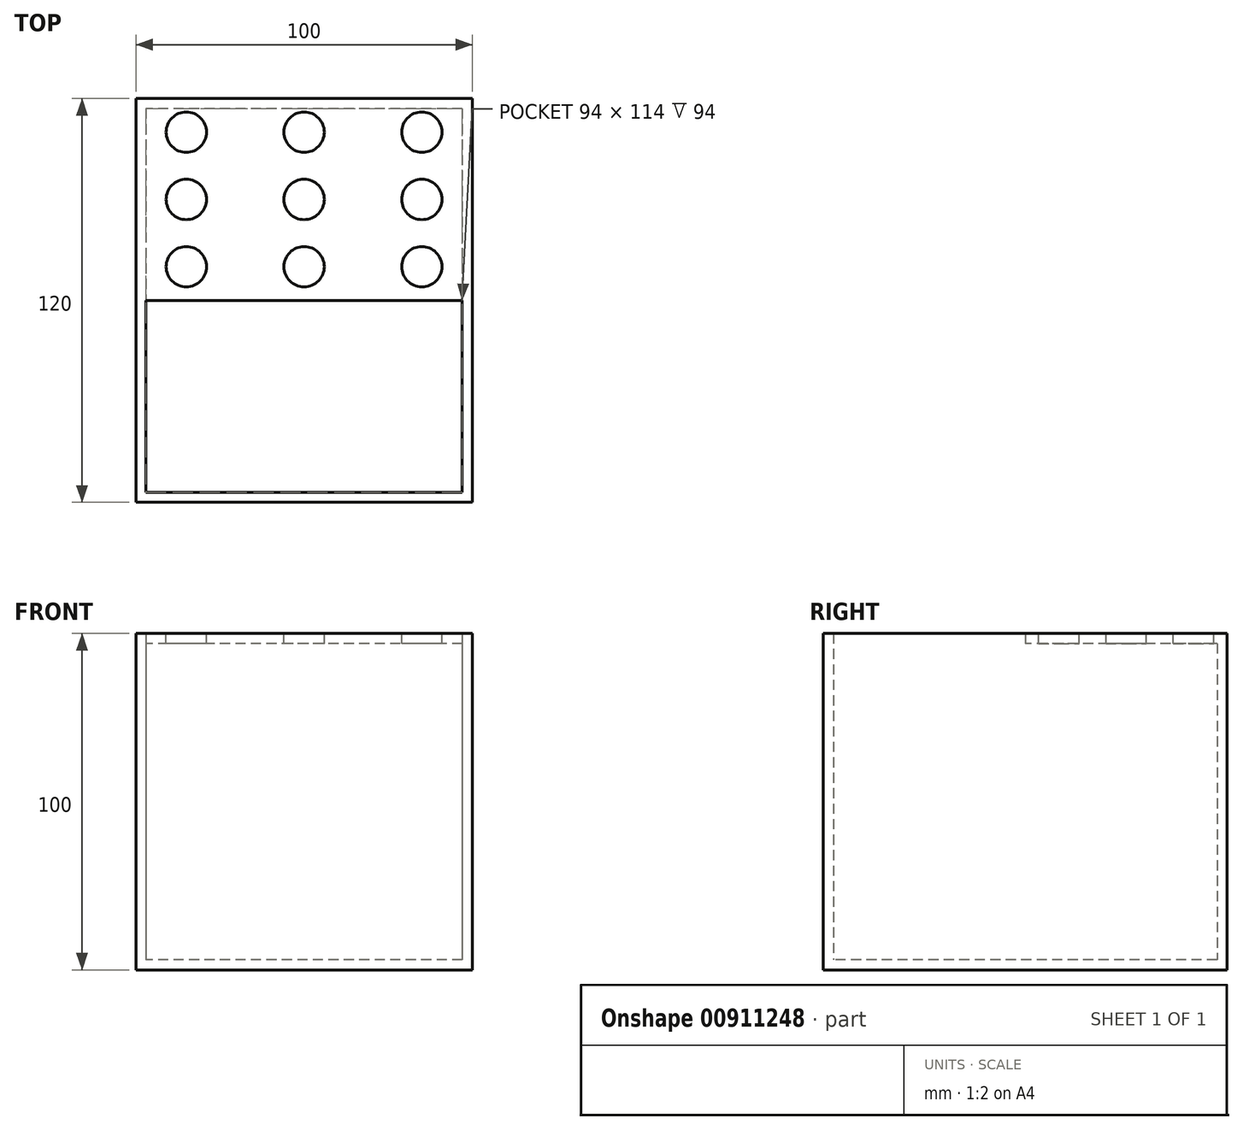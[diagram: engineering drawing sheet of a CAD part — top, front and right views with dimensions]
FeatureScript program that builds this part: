
annotation { "Feature Type Name" : "Feature", "Feature Type Description" : "" }
export const myFeature = defineFeature(function(context is Context, id is Id, definition is map)
    precondition{}
    {
        {
            var Q0;
            Q0=qCreatedBy(makeId("Top.planeOp"),FACE);
            var sketch = newSketch(context, id + "F0", { "sketchPlane" : qUnion([Q0])});
            skLineSegment(sketch, "E0.bottom", {"start": v(50, 60) * mm, "end": v(-50, 60) * mm});
            skLineSegment(sketch, "E0.top", {"start": v(50, -60) * mm, "end": v(-50, -60) * mm});
            skLineSegment(sketch, "E0.left", {"start": v(50, 60) * mm, "end": v(50, -60) * mm});
            skLineSegment(sketch, "E0.right", {"start": v(-50, 60) * mm, "end": v(-50, -60) * mm});
            skPoint(sketch, "E0.middle", {"position": v(0, 0) * mm});
            skSolve(sketch);
        }
        {
            var Q0;
            Q0 = qSketchRegion(id + "F0", true);
            extrude(context, id + "F1", {"entities" : qUnion([Q0]), "depth" : 100 * mm, "offsetDistance" : 25 * mm});
        }
        {
            var Q0;
            Q0=makeQuery(id+"F1.opExtrude","CAP_FACE",FACE,{"disambiguationData":[OSD([sQuery(id+"F0.wireOp",EDGE,"E0.bottom"),sQuery(id+"F0.wireOp",EDGE,"E0.top"),sQuery(id+"F0.wireOp",EDGE,"E0.left"),sQuery(id+"F0.wireOp",EDGE,"E0.right")])],"isStart":false});
            shell(context, id + "F2", {"entities" : qUnion([Q0]), "thickness" : 3 * mm});
        }
        {
            var Q0;
            Q0=makeQuery(id+"F1.opExtrude","CAP_FACE",FACE,{"disambiguationData":[OSD([sQuery(id+"F0.wireOp",EDGE,"E0.bottom"),sQuery(id+"F0.wireOp",EDGE,"E0.top"),sQuery(id+"F0.wireOp",EDGE,"E0.left"),sQuery(id+"F0.wireOp",EDGE,"E0.right")])],"isStart":false});
            var sketch = newSketch(context, id + "F3", { "sketchPlane" : qUnion([Q0])});
            skPoint(sketch, "E1.0", {"position": v(-50, 60) * mm});
            skLineSegment(sketch, "E2.bottom", {"start": v(-50, 60) * mm, "end": v(50, 60) * mm});
            skLineSegment(sketch, "E2.top", {"start": v(-50, 0) * mm, "end": v(50, 0) * mm});
            skLineSegment(sketch, "E2.left", {"start": v(-50, 60) * mm, "end": v(-50, 0) * mm});
            skLineSegment(sketch, "E2.right", {"start": v(50, 60) * mm, "end": v(50, 0) * mm});
            skSolve(sketch);
        }
        {
            var Q0;
            Q0 = qSketchRegion(id + "F3", true);
            extrude(context, id + "F4", {"entities" : qUnion([Q0]), "operationType" : NewBodyOperationType.ADD, "oppositeDirection" : true, "depth" : 3 * mm, "offsetDistance" : 25 * mm});
        }
        {
            var Q0;
            Q0=makeQuery(id+"F4.boolean.opBoolean","MERGE",FACE,{"derivedFrom":[makeQuery(id+"F1.opExtrude","CAP_FACE",FACE,{"disambiguationData":[OSD([sQuery(id+"F0.wireOp",EDGE,"E0.bottom"),sQuery(id+"F0.wireOp",EDGE,"E0.top"),sQuery(id+"F0.wireOp",EDGE,"E0.left"),sQuery(id+"F0.wireOp",EDGE,"E0.right")])],"isStart":false}),makeQuery(id+"F4.opExtrude","CAP_FACE",FACE,{"disambiguationData":[OSD([sQuery(id+"F3.wireOp",EDGE,"E2.bottom"),sQuery(id+"F3.wireOp",EDGE,"E2.top"),sQuery(id+"F3.wireOp",EDGE,"E2.left"),sQuery(id+"F3.wireOp",EDGE,"E2.right")])],"isStart":true})]});
            var sketch = newSketch(context, id + "F5", { "sketchPlane" : qUnion([Q0])});
            skCircle(sketch, "E3", {"center": v(0, 30) * mm, "radius": 6 * mm});
            skLineSegment(sketch, "E4", {"start": v(0, 60) * mm, "end": v(0, 0) * mm, "construction": true});
            skCircle(sketch, "E5", {"center": v(35, 30) * mm, "radius": 6 * mm});
            skCircle(sketch, "E6.MirrorC", {"center": v(-35, 30) * mm, "radius": 6 * mm});
            skCircle(sketch, "E7.0.1.0", {"center": v(-35, 50) * mm, "radius": 6 * mm});
            skCircle(sketch, "E7.0.1.1", {"center": v(0, 50) * mm, "radius": 6 * mm});
            skCircle(sketch, "E7.0.1.2", {"center": v(35, 50) * mm, "radius": 6 * mm});
            skLineSegment(sketch, "E7.direction1", {"start": v(-35, 30) * mm, "end": v(-10, 30) * mm, "construction": true});
            skLineSegment(sketch, "E7.direction2", {"start": v(-35, 30) * mm, "end": v(-35, 50) * mm, "construction": true});
            skCircle(sketch, "E8.0.1.0", {"center": v(-35, 10) * mm, "radius": 6 * mm});
            skCircle(sketch, "E8.0.1.1", {"center": v(0, 10) * mm, "radius": 6 * mm});
            skCircle(sketch, "E8.0.1.2", {"center": v(35, 10) * mm, "radius": 6 * mm});
            skLineSegment(sketch, "E8.direction2", {"start": v(-35, 30) * mm, "end": v(-35, 10) * mm, "construction": true});
            skSolve(sketch);
        }
        {
            var Q0;
            Q0 = qSketchRegion(id + "F5", true);
            extrude(context, id + "F6", {"entities" : qUnion([Q0]), "operationType" : NewBodyOperationType.REMOVE, "oppositeDirection" : true, "depth" : 25 * mm, "offsetDistance" : 25 * mm});
        }
    });
